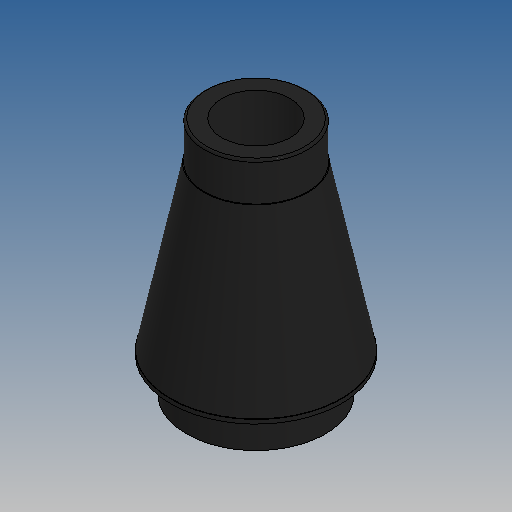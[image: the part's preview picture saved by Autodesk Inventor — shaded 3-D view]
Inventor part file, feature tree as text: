
AUTODESK INVENTOR PART (.ipt)
format: ipt  version: 2025.1 (Build 291241000, 241)  size: 192,512 bytes
history: native  units: in
note: dims shown in document units (in); Inventor stores cm internally (conversion verified against a paired STEP export)
features: sketch x2, revolve x1, fillet x1, extrude x1
ambient origin geometry x8: Origin, YZ Plane, XZ Plane, XY Plane, X Axis, Y Axis, Z Axis, Center Point
bodies: Solid2 (feature_tree)
feature tree (5):
  revolve  "Revolution1"  [1 undecoded]
  fillet  "Fillet1"  Radius=0.063in
  extrude  "Extrusion7"  Depth=0.0709in
  sketch  "Sketch11"  dims[d7=0.0591in d22=0.0039in d99=0.189in d100=0.063in]
  sketch  "Sketch12"  dims[d101=0.2564in d102=0.315in d104=0.126in d105=0.189in d106=0.063in d107=0.378in d108=90.0deg d109=0.1417in d110=0.0079in d111=0.063in d112=0.0709in d113=0.0in d114=0.0in d115=0.0in d116=0.0709in]
note: 1 required parameter value undecoded (feature->parameter linkage not recoverable at this tier; creation-order binding heuristic only, values carry confidence <= 0.55)
